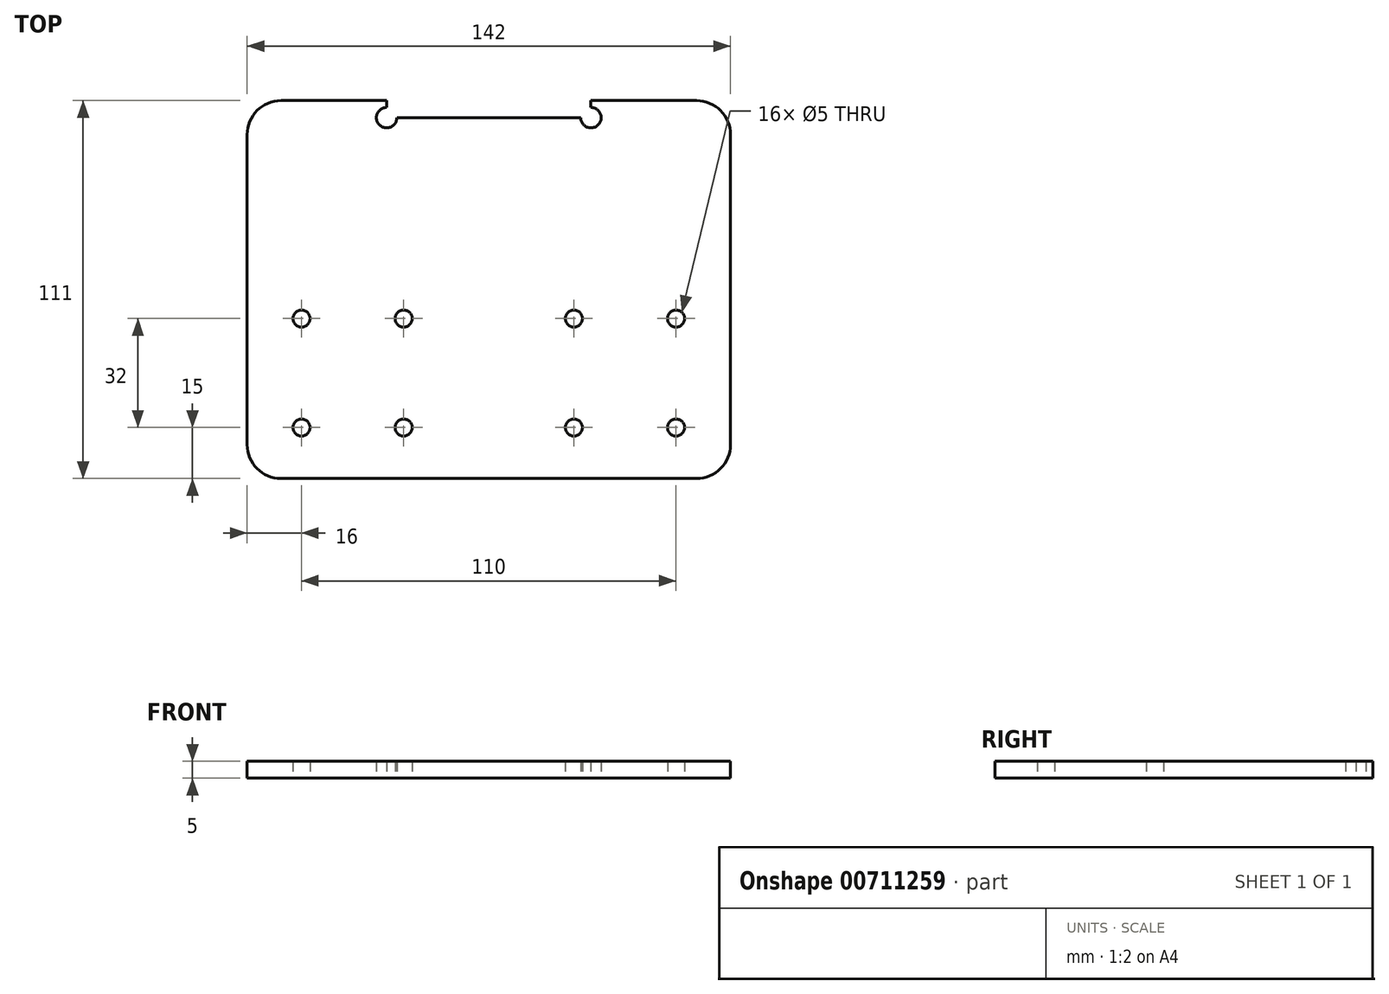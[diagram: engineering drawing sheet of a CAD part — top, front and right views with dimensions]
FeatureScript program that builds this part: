
annotation { "Feature Type Name" : "Feature", "Feature Type Description" : "" }
export const myFeature = defineFeature(function(context is Context, id is Id, definition is map)
    precondition{}
    {
        {
            var Q0;
            Q0=qCreatedBy(makeId("Top.planeOp"),FACE);
            var sketch = newSketch(context, id + "F0", { "sketchPlane" : qUnion([Q0])});
            skPoint(sketch, "E0.middle", {"position": v(0, 0) * mm});
            skCircle(sketch, "E1", {"center": v(-55, -10.5) * mm, "radius": 2.5 * mm});
            skCircle(sketch, "E2", {"center": v(-55, -42.5) * mm, "radius": 2.5 * mm});
            skCircle(sketch, "E3", {"center": v(-25, -10.5) * mm, "radius": 2.5 * mm});
            skCircle(sketch, "E4", {"center": v(-25, -42.5) * mm, "radius": 2.5 * mm});
            skCircle(sketch, "E5.MirrorC", {"center": v(25, -10.5) * mm, "radius": 2.5 * mm});
            skCircle(sketch, "E6.MirrorC", {"center": v(55, -42.5) * mm, "radius": 2.5 * mm});
            skCircle(sketch, "E7.MirrorC", {"center": v(55, -10.5) * mm, "radius": 2.5 * mm});
            skCircle(sketch, "E8.MirrorC", {"center": v(25, -42.5) * mm, "radius": 2.5 * mm});
            skLineSegment(sketch, "E9.0", {"start": v(27, 48.5) * mm, "end": v(-27, 48.5) * mm});
            skLineSegment(sketch, "E10.0", {"start": v(30, 51.5) * mm, "end": v(30, 53.5) * mm});
            skLineSegment(sketch, "E11", {"start": v(-30, 51.5) * mm, "end": v(-30, 53.5) * mm});
            skArc(sketch, "E12", {"start": v(-30, 51.5) * mm, "mid": v(-32.12, 46.38) * mm, "end": v(-27, 48.5) * mm});
            skArc(sketch, "E13.MirrorCS", {"start": v(30, 51.5) * mm, "mid": v(32.12, 46.38) * mm, "end": v(27, 48.5) * mm});
            skLineSegment(sketch, "E14.bottom", {"start": v(61, 53.5) * mm, "end": v(30, 53.5) * mm});
            skLineSegment(sketch, "E14.top", {"start": v(61, -57.5) * mm, "end": v(-61, -57.5) * mm});
            skLineSegment(sketch, "E14.left", {"start": v(71, 43.5) * mm, "end": v(71, -47.5) * mm});
            skLineSegment(sketch, "E14.right", {"start": v(-71, 43.5) * mm, "end": v(-71, -47.5) * mm});
            skPoint(sketch, "E14.middle", {"position": v(0, -2) * mm});
            skPoint(sketch, "E15.visualSharp", {"position": v(-71, 53.5) * mm});
            skArc(sketch, "E15.filletArc", {"start": v(-61, 53.5) * mm, "mid": v(-68.07, 50.57) * mm, "end": v(-71, 43.5) * mm});
            skPoint(sketch, "E16.visualSharp", {"position": v(71, 53.5) * mm});
            skArc(sketch, "E16.filletArc", {"start": v(71, 43.5) * mm, "mid": v(68.07, 50.57) * mm, "end": v(61, 53.5) * mm});
            skPoint(sketch, "E17.visualSharp", {"position": v(71, -57.5) * mm});
            skArc(sketch, "E17.filletArc", {"start": v(61, -57.5) * mm, "mid": v(68.07, -54.57) * mm, "end": v(71, -47.5) * mm});
            skPoint(sketch, "E18.visualSharp", {"position": v(-71, -57.5) * mm});
            skArc(sketch, "E18.filletArc", {"start": v(-71, -47.5) * mm, "mid": v(-68.07, -54.57) * mm, "end": v(-61, -57.5) * mm});
            skLineSegment(sketch, "E19.trimOffspring", {"start": v(-30, 53.5) * mm, "end": v(-61, 53.5) * mm});
            skSolve(sketch);
        }
        {
            var Q0;
            Q0=makeQuery(id+"F0.imprint","IMPRINT",FACE,{"disambiguationData":[TD([[makeQuery(id+"F0.imprint","IMPRINT",EDGE,{"derivedFrom":sQuery(id+"F0.wireOp",EDGE,"E1")}),-1.0]])]});
            extrude(context, id + "F1", {"entities" : qUnion([Q0]), "depth" : 5 * mm, "offsetDistance" : 25 * mm});
        }
    });
